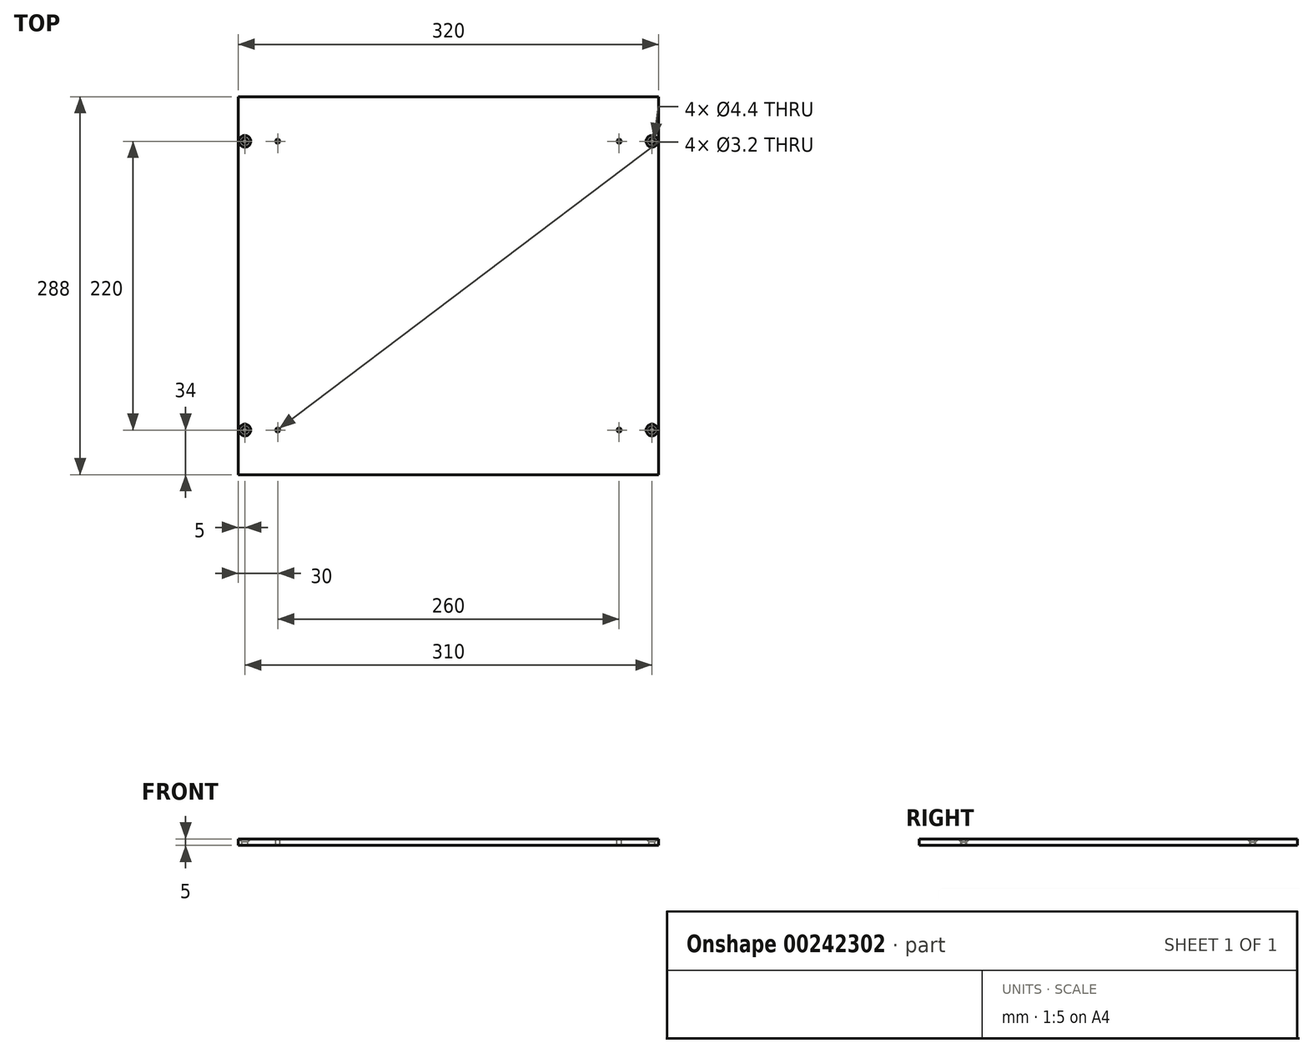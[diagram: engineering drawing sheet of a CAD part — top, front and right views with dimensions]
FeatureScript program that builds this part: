
annotation { "Feature Type Name" : "Feature", "Feature Type Description" : "" }
export const myFeature = defineFeature(function(context is Context, id is Id, definition is map)
    precondition{}
    {
        {
            var Q0;
            Q0=qCreatedBy(makeId("Top.planeOp"),FACE);
            var sketch = newSketch(context, id + "F0", { "sketchPlane" : qUnion([Q0])});
            skLineSegment(sketch, "E0.bottom", {"start": v(160, -144) * mm, "end": v(-160, -144) * mm});
            skLineSegment(sketch, "E0.top", {"start": v(160, 144) * mm, "end": v(-160, 144) * mm});
            skLineSegment(sketch, "E0.left", {"start": v(160, -144) * mm, "end": v(160, 144) * mm});
            skLineSegment(sketch, "E0.right", {"start": v(-160, -144) * mm, "end": v(-160, 144) * mm});
            skPoint(sketch, "E0.middle", {"position": v(0, 0) * mm});
            skSolve(sketch);
        }
        {
            var Q0;
            Q0 = qSketchRegion(id + "F0", true);
            extrude(context, id + "F1", {"entities" : qUnion([Q0]), "endBound" : BoundingType.SYMMETRIC, "depth" : 5 * mm});
        }
        {
            var Q0;
            Q0=makeQuery(id+"F1.opExtrude","CAP_FACE",FACE,{"disambiguationData":[OSD([sQuery(id+"F0.wireOp",EDGE,"E0.bottom"),sQuery(id+"F0.wireOp",EDGE,"E0.top"),sQuery(id+"F0.wireOp",EDGE,"E0.left"),sQuery(id+"F0.wireOp",EDGE,"E0.right")])],"isStart":false});
            var sketch = newSketch(context, id + "F2", { "sketchPlane" : qUnion([Q0])});
            skCircle(sketch, "E1", {"center": v(-155, -110) * mm, "radius": 2 * mm});
            skCircle(sketch, "E2.MirrorC", {"center": v(155, -110) * mm, "radius": 2 * mm});
            skCircle(sketch, "E3.MirrorC", {"center": v(-155, 110) * mm, "radius": 2 * mm});
            skCircle(sketch, "E4.MirrorC", {"center": v(155, 110) * mm, "radius": 2 * mm});
            skSolve(sketch);
        }
        {
            var Q0;
            Q0=sQuery(id+"F2.wireOp",VERTEX,"E1.center");
            var Q1;
            Q1=sQuery(id+"F2.wireOp",VERTEX,"E2.MirrorC.center");
            var Q2;
            Q2=sQuery(id+"F2.wireOp",VERTEX,"E4.MirrorC.center");
            var Q3;
            Q3=sQuery(id+"F2.wireOp",VERTEX,"E3.MirrorC.center");
            var Q4;
            Q4=makeQuery(id+"F1.opExtrude","SWEPT_BODY",BODY,{"disambiguationData":[OSD([sQuery(id+"F0.wireOp",EDGE,"E0.bottom"),sQuery(id+"F0.wireOp",EDGE,"E0.top"),sQuery(id+"F0.wireOp",EDGE,"E0.left"),sQuery(id+"F0.wireOp",EDGE,"E0.right")])]});
            hole(context, id + "F3", {"style" : HoleStyle.C_SINK, "endStyle" : HoleEndStyle.BLIND, "standardTappedOrClearance" : lookupTablePath({ "standard" : "ISO", "fit" : "Normal", "size" : "M4", "type" : "Clearance" }), "standardBlindInLast" : lookupTablePath({ "fit" : "Standard", "standard" : "ISO", "size" : "M4", "type" : "Clearance" }), "holeDiameter" : 4.4 * mm, "cSinkDiameter" : 8.96 * mm, "cSinkAngle" : 90 * degree, "holeDepth" : 17.25 * mm, "tappedDepth" : 15 * mm, "tapClearance" : 3, "locations" : qUnion([Q0, Q1, Q2, Q3]), "scope" : qUnion([Q4])});
        }
        {
            var Q0;
            Q0=makeQuery(id+"F1.opExtrude","CAP_FACE",FACE,{"disambiguationData":[OSD([sQuery(id+"F0.wireOp",EDGE,"E0.bottom"),sQuery(id+"F0.wireOp",EDGE,"E0.top"),sQuery(id+"F0.wireOp",EDGE,"E0.left"),sQuery(id+"F0.wireOp",EDGE,"E0.right")])],"isStart":false});
            var sketch = newSketch(context, id + "F4", { "sketchPlane" : qUnion([Q0])});
            skCircle(sketch, "E5", {"center": v(-130, -110) * mm, "radius": 2 * mm});
            skCircle(sketch, "E6.MirrorC", {"center": v(130, -110) * mm, "radius": 2 * mm});
            skCircle(sketch, "E7.MirrorC", {"center": v(-130, 110) * mm, "radius": 2 * mm});
            skCircle(sketch, "E8.MirrorC", {"center": v(130, 110) * mm, "radius": 2 * mm});
            skSolve(sketch);
        }
        {
            var Q0;
            Q0=sQuery(id+"F4.wireOp",VERTEX,"E5.center");
            var Q1;
            Q1=sQuery(id+"F4.wireOp",VERTEX,"E7.MirrorC.center");
            var Q2;
            Q2=sQuery(id+"F4.wireOp",VERTEX,"E8.MirrorC.center");
            var Q3;
            Q3=sQuery(id+"F4.wireOp",VERTEX,"E6.MirrorC.center");
            var Q4;
            Q4=makeQuery(id+"F1.opExtrude","SWEPT_BODY",BODY,{"disambiguationData":[OSD([sQuery(id+"F0.wireOp",EDGE,"E0.bottom"),sQuery(id+"F0.wireOp",EDGE,"E0.top"),sQuery(id+"F0.wireOp",EDGE,"E0.left"),sQuery(id+"F0.wireOp",EDGE,"E0.right")])]});
            hole(context, id + "F5", {"style" : HoleStyle.SIMPLE, "endStyle" : HoleEndStyle.THROUGH, "standardTappedOrClearance" : lookupTablePath({ "standard" : "ISO", "engagement" : "75%", "pitch" : "0.75 mm", "size" : "M4", "type" : "Tapped" }), "standardBlindInLast" : lookupTablePath({ "standard" : "ISO", "engagement" : "75%", "pitch" : "0.75 mm", "size" : "M4", "type" : "Tapped" }), "holeDiameter" : 3.2 * mm, "showTappedDepth" : true, "tappedDepth" : 15 * mm, "tapClearance" : 3, "locations" : qUnion([Q0, Q1, Q2, Q3]), "scope" : qUnion([Q4])});
        }
    });
